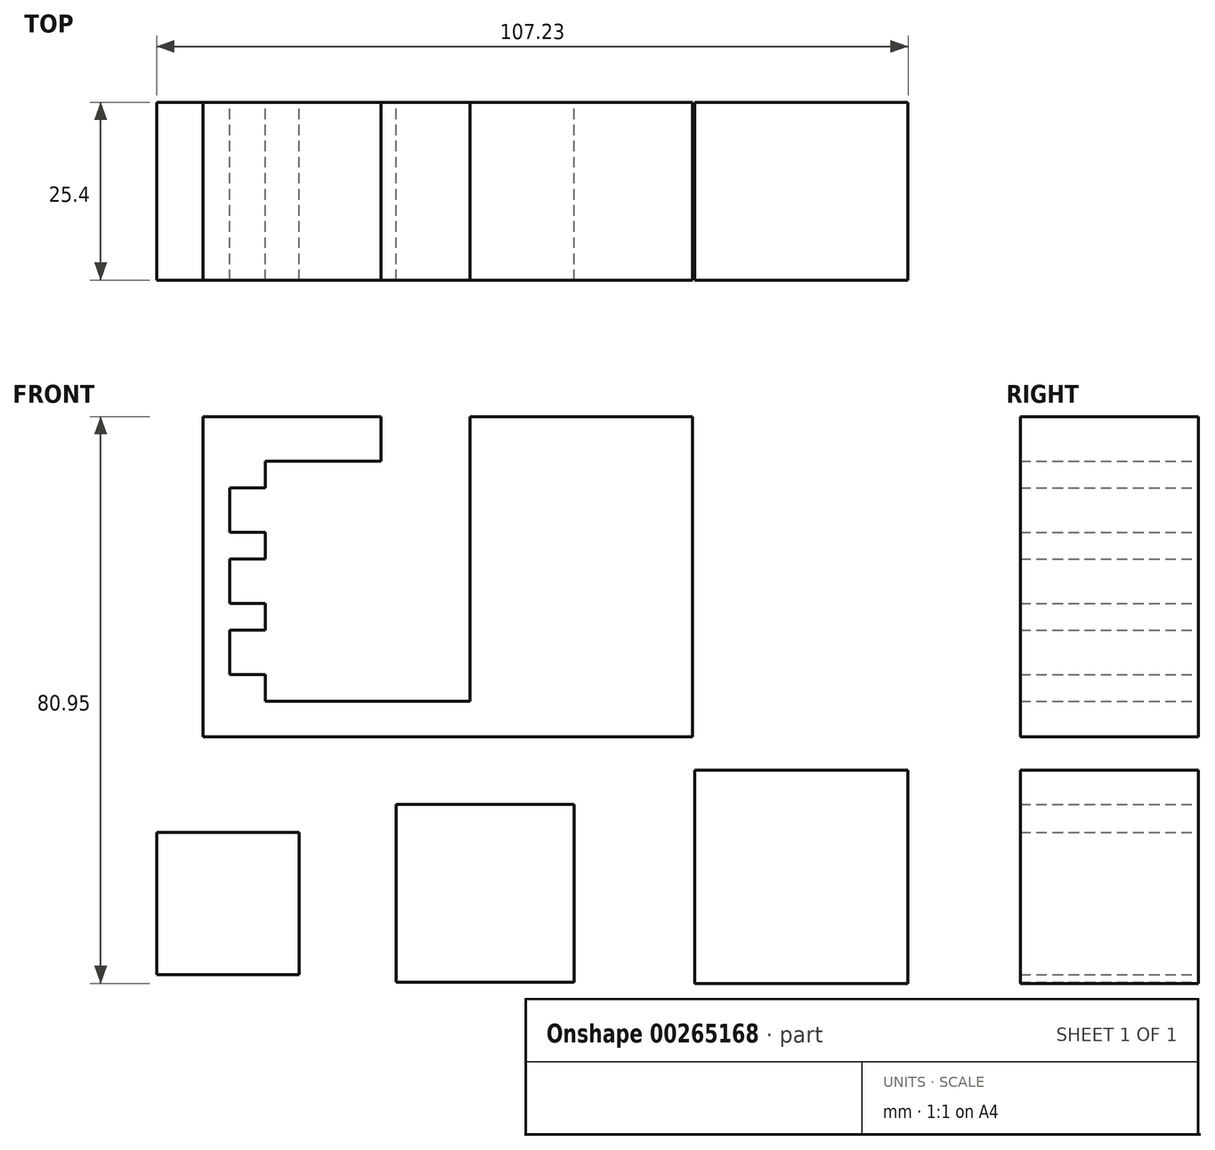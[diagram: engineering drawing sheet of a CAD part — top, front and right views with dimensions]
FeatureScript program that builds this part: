
annotation { "Feature Type Name" : "Feature", "Feature Type Description" : "" }
export const myFeature = defineFeature(function(context is Context, id is Id, definition is map)
    precondition{}
    {
        {
            var Q0;
            Q0=qCreatedBy(makeId("Front.planeOp"),FACE);
            var sketch = newSketch(context, id + "F0", { "sketchPlane" : qUnion([Q0])});
            skLineSegment(sketch, "E0", {"start": v(-59.49, 40.64) * mm, "end": v(-34.09, 40.64) * mm});
            skLineSegment(sketch, "E1", {"start": v(-34.09, 40.64) * mm, "end": v(-34.09, 34.29) * mm});
            skLineSegment(sketch, "E2", {"start": v(-34.09, 34.29) * mm, "end": v(-50.6, 34.29) * mm});
            skLineSegment(sketch, "E3", {"start": v(-50.6, 34.29) * mm, "end": v(-50.6, 30.48) * mm});
            skLineSegment(sketch, "E4", {"start": v(-50.6, 30.48) * mm, "end": v(-55.67, 30.48) * mm});
            skLineSegment(sketch, "E5", {"start": v(-55.67, 30.48) * mm, "end": v(-55.67, 24.13) * mm});
            skLineSegment(sketch, "E6", {"start": v(-55.67, 24.13) * mm, "end": v(-50.6, 24.13) * mm});
            skLineSegment(sketch, "E7", {"start": v(-50.6, 24.13) * mm, "end": v(-50.6, 20.32) * mm});
            skLineSegment(sketch, "E8", {"start": v(-50.6, 20.32) * mm, "end": v(-55.67, 20.32) * mm});
            skLineSegment(sketch, "E9", {"start": v(-55.67, 20.32) * mm, "end": v(-55.67, 13.97) * mm});
            skLineSegment(sketch, "E10", {"start": v(-55.67, 13.97) * mm, "end": v(-50.6, 13.97) * mm});
            skLineSegment(sketch, "E11", {"start": v(-50.6, 13.97) * mm, "end": v(-50.6, 10.16) * mm});
            skLineSegment(sketch, "E12", {"start": v(-50.6, 10.16) * mm, "end": v(-55.67, 10.16) * mm});
            skLineSegment(sketch, "E13", {"start": v(-55.67, 10.16) * mm, "end": v(-55.67, 3.8) * mm});
            skLineSegment(sketch, "E14", {"start": v(-55.67, 3.8) * mm, "end": v(-50.6, 3.81) * mm});
            skLineSegment(sketch, "E15", {"start": v(-21.35, 6.6) * mm, "end": v(-21.35, 40.64) * mm});
            skLineSegment(sketch, "E16", {"start": v(-21.35, 40.64) * mm, "end": v(10.4, 40.64) * mm});
            skPoint(sketch, "E17.end.orphan", {"position": v(10.4, 6.35) * mm});
            skLineSegment(sketch, "E18", {"start": v(10.4, 40.64) * mm, "end": v(10.4, 0) * mm});
            skPoint(sketch, "E19.start.orphan", {"position": v(-34.09, 6.35) * mm});
            skPoint(sketch, "E20.start.orphan", {"position": v(-34.09, 0) * mm});
            skLineSegment(sketch, "E21", {"start": v(-50.6, 3.81) * mm, "end": v(-50.6, 0) * mm});
            skLineSegment(sketch, "E22", {"start": v(-50.6, 0) * mm, "end": v(-21.35, 0) * mm});
            skLineSegment(sketch, "E23", {"start": v(-21.35, 0) * mm, "end": v(-21.35, 6.6) * mm});
            skLineSegment(sketch, "E24", {"start": v(10.4, 0) * mm, "end": v(10.4, -5.09) * mm});
            skLineSegment(sketch, "E25", {"start": v(10.4, -5.09) * mm, "end": v(-59.49, -5.09) * mm});
            skPoint(sketch, "E26.start.orphan", {"position": v(-59.49, 0) * mm});
            skLineSegment(sketch, "E27", {"start": v(-59.49, 40.64) * mm, "end": v(-59.49, -5.09) * mm});
            skSolve(sketch);
        }
        {
            var Q0;
            Q0=qCreatedBy(makeId("Front.planeOp"),FACE);
            var sketch = newSketch(context, id + "F1", { "sketchPlane" : qUnion([Q0])});
            skLineSegment(sketch, "E28.bottom", {"start": v(-66.08, -18.73) * mm, "end": v(-45.76, -18.73) * mm});
            skLineSegment(sketch, "E28.top", {"start": v(-66.08, -39.05) * mm, "end": v(-45.76, -39.05) * mm});
            skLineSegment(sketch, "E28.left", {"start": v(-66.08, -18.73) * mm, "end": v(-66.08, -39.05) * mm});
            skLineSegment(sketch, "E28.right", {"start": v(-45.76, -18.73) * mm, "end": v(-45.76, -39.05) * mm});
            skSolve(sketch);
        }
        {
            var Q0;
            Q0=qCreatedBy(makeId("Front.planeOp"),FACE);
            var sketch = newSketch(context, id + "F2", { "sketchPlane" : qUnion([Q0])});
            skLineSegment(sketch, "E29.bottom", {"start": v(-31.94, -14.76) * mm, "end": v(-6.54, -14.76) * mm});
            skLineSegment(sketch, "E29.top", {"start": v(-31.94, -40.16) * mm, "end": v(-6.54, -40.16) * mm});
            skLineSegment(sketch, "E29.left", {"start": v(-31.94, -14.76) * mm, "end": v(-31.94, -40.16) * mm});
            skLineSegment(sketch, "E29.right", {"start": v(-6.54, -14.76) * mm, "end": v(-6.54, -40.16) * mm});
            skSolve(sketch);
        }
        {
            var Q0;
            Q0=qCreatedBy(makeId("Front.planeOp"),FACE);
            var sketch = newSketch(context, id + "F3", { "sketchPlane" : qUnion([Q0])});
            skLineSegment(sketch, "E30.bottom", {"start": v(10.67, -40.31) * mm, "end": v(41.15, -40.31) * mm});
            skLineSegment(sketch, "E30.top", {"start": v(10.67, -9.83) * mm, "end": v(41.15, -9.83) * mm});
            skLineSegment(sketch, "E30.left", {"start": v(10.67, -40.31) * mm, "end": v(10.67, -9.83) * mm});
            skLineSegment(sketch, "E30.right", {"start": v(41.15, -40.31) * mm, "end": v(41.15, -9.83) * mm});
            skSolve(sketch);
        }
        {
            var Q0;
            Q0=makeQuery(id+"F0.imprint","IMPRINT",FACE,{"disambiguationData":[TD([[makeQuery(id+"F0.imprint","IMPRINT",EDGE,{"derivedFrom":sQuery(id+"F0.wireOp",EDGE,"E0")}),-1.0]])]});
            extrude(context, id + "F4", {"entities" : qUnion([Q0]), "depth" : 25.4 * mm});
        }
        {
            var Q0;
            Q0=makeQuery(id+"F1.imprint","IMPRINT",FACE,{"disambiguationData":[TD([[makeQuery(id+"F1.imprint","IMPRINT",EDGE,{"derivedFrom":sQuery(id+"F1.wireOp",EDGE,"E28.bottom")}),-1.0]])]});
            extrude(context, id + "F5", {"entities" : qUnion([Q0]), "depth" : 25.4 * mm});
        }
        {
            var Q0;
            Q0=makeQuery(id+"F2.imprint","IMPRINT",FACE,{"disambiguationData":[TD([[makeQuery(id+"F2.imprint","IMPRINT",EDGE,{"derivedFrom":sQuery(id+"F2.wireOp",EDGE,"E29.bottom")}),-1.0]])]});
            extrude(context, id + "F6", {"entities" : qUnion([Q0]), "depth" : 25.4 * mm});
        }
        {
            var Q0;
            Q0=makeQuery(id+"F3.imprint","IMPRINT",FACE,{"disambiguationData":[TD([[makeQuery(id+"F3.imprint","IMPRINT",EDGE,{"derivedFrom":sQuery(id+"F3.wireOp",EDGE,"E30.bottom")}),1.0]])]});
            extrude(context, id + "F7", {"entities" : qUnion([Q0]), "depth" : 25.4 * mm});
        }
    });
